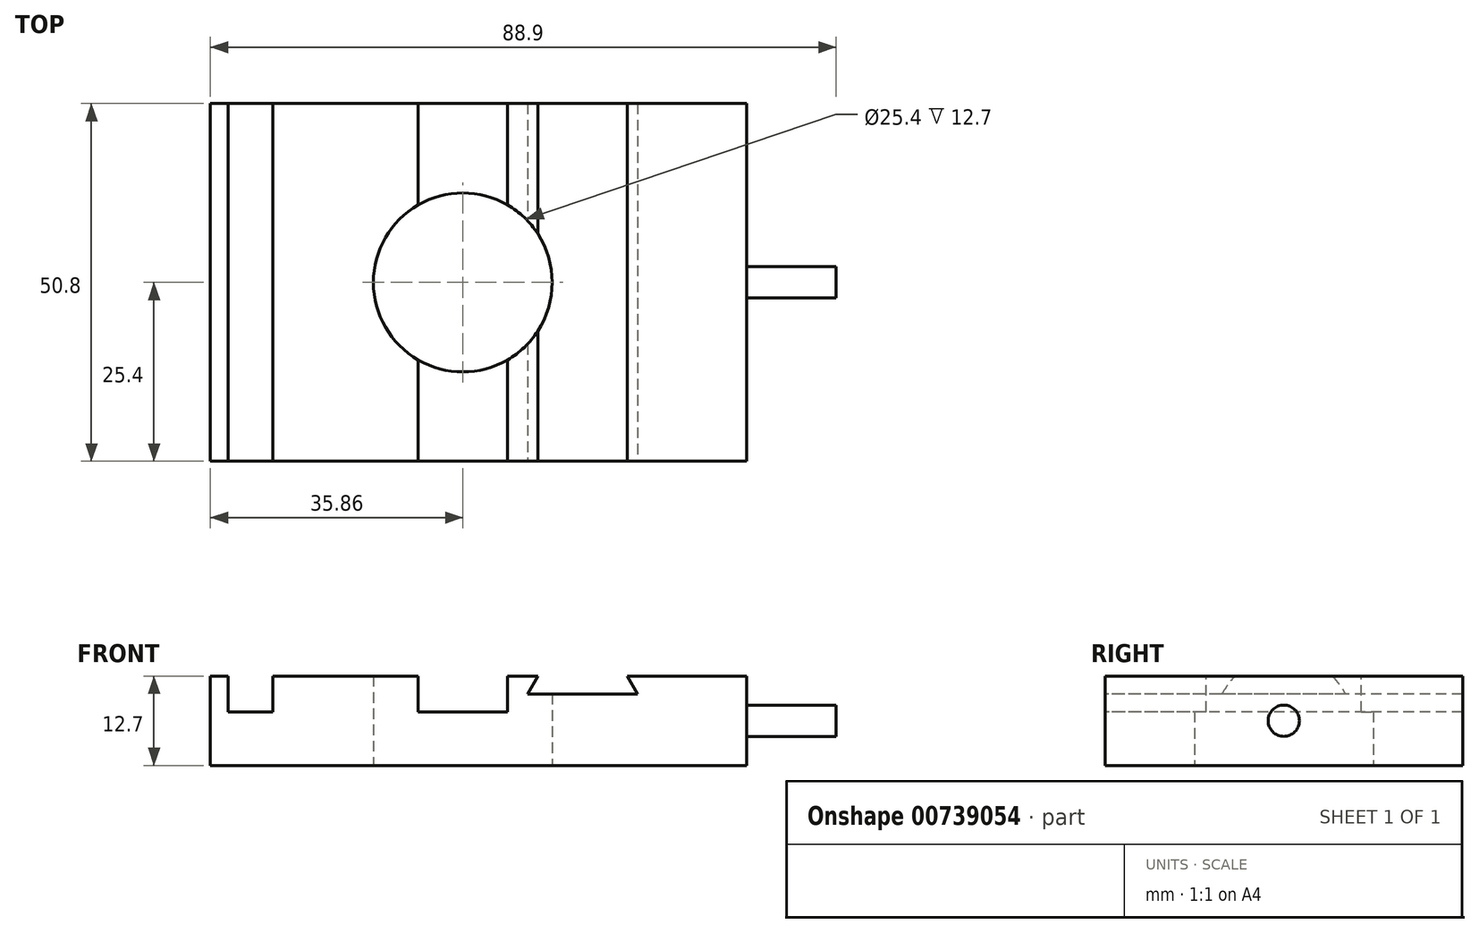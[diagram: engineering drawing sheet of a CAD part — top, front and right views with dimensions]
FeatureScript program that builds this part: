
annotation { "Feature Type Name" : "Feature", "Feature Type Description" : "" }
export const myFeature = defineFeature(function(context is Context, id is Id, definition is map)
    precondition{}
    {
        {
            var Q0;
            Q0=qCreatedBy(makeId("Top.planeOp"),FACE);
            var sketch = newSketch(context, id + "F0", { "sketchPlane" : qUnion([Q0])});
            skLineSegment(sketch, "E0.bottom", {"start": v(40.34, 25.4) * mm, "end": v(-35.86, 25.4) * mm});
            skLineSegment(sketch, "E0.top", {"start": v(40.34, -25.4) * mm, "end": v(-35.86, -25.4) * mm});
            skLineSegment(sketch, "E0.left", {"start": v(40.34, 25.4) * mm, "end": v(40.34, -25.4) * mm});
            skLineSegment(sketch, "E0.right", {"start": v(-35.86, 25.4) * mm, "end": v(-35.86, -25.4) * mm});
            skCircle(sketch, "E1", {"center": v(0, 0) * mm, "radius": 12.7 * mm});
            skSolve(sketch);
        }
        {
            var Q0;
            Q0=makeQuery(id+"F0.imprint","IMPRINT",FACE,{"disambiguationData":[TD([[makeQuery(id+"F0.imprint","IMPRINT",EDGE,{"derivedFrom":sQuery(id+"F0.wireOp",EDGE,"E0.bottom")}),1.0]])]});
            extrude(context, id + "F1", {"entities" : qUnion([Q0]), "depth" : 12.7 * mm, "offsetDistance" : 25 * mm});
        }
        {
            var Q0;
            Q0=makeQuery(id+"F1.opExtrude","CAP_FACE",FACE,{"disambiguationData":[OSD([sQuery(id+"F0.wireOp",EDGE,"E0.bottom"),sQuery(id+"F0.wireOp",EDGE,"E0.top"),sQuery(id+"F0.wireOp",EDGE,"E0.left"),sQuery(id+"F0.wireOp",EDGE,"E0.right"),sQuery(id+"F0.wireOp",EDGE,"E1")])],"isStart":false});
            var sketch = newSketch(context, id + "F2", { "sketchPlane" : qUnion([Q0])});
            skLineSegment(sketch, "E2.bottom", {"start": v(-33.32, 25.4) * mm, "end": v(-26.97, 25.4) * mm});
            skLineSegment(sketch, "E2.top", {"start": v(-33.32, -25.4) * mm, "end": v(-26.97, -25.4) * mm});
            skLineSegment(sketch, "E2.left", {"start": v(-33.32, 25.4) * mm, "end": v(-33.32, -25.4) * mm});
            skLineSegment(sketch, "E2.right", {"start": v(-26.97, 25.4) * mm, "end": v(-26.97, -25.4) * mm});
            skLineSegment(sketch, "E3", {"start": v(-6.35, 25.4) * mm, "end": v(-6.35, -25.4) * mm});
            skLineSegment(sketch, "E4", {"start": v(-6.35, -25.4) * mm, "end": v(6.35, -25.4) * mm});
            skLineSegment(sketch, "E5", {"start": v(6.35, -25.4) * mm, "end": v(6.35, 25.4) * mm});
            skPoint(sketch, "E6", {"position": v(0, 0) * mm});
            skLineSegment(sketch, "E7", {"start": v(6.35, 25.4) * mm, "end": v(-6.35, 25.4) * mm, "construction": true});
            skLineSegment(sketch, "E8", {"start": v(6.35, 25.4) * mm, "end": v(-6.35, 25.4) * mm});
            skLineSegment(sketch, "E9", {"start": v(0, 25.4) * mm, "end": v(0, -25.4) * mm, "construction": true});
            skSolve(sketch);
        }
        {
            var Q0;
            Q0=makeQuery(id+"F2.imprint","IMPRINT",FACE,{"disambiguationData":[TD([[makeQuery(id+"F2.imprint","IMPRINT",EDGE,{"derivedFrom":sQuery(id+"F2.wireOp",EDGE,"E2.bottom")}),1.0]])]});
            var Q1;
            {var subQ0=sQuery(id+"F2.wireOp",EDGE,"E4");Q1=makeQuery(id+"F2.imprint","IMPRINT",FACE,{"disambiguationData":[TD([[makeQuery(id+"F2.imprint","IMPRINT",EDGE,{"derivedFrom":subQ0}),-1.0]])]});}
            var Q2;
            {var subQ0=sQuery(id+"F2.wireOp",EDGE,"E8");Q2=makeQuery(id+"F2.imprint","IMPRINT",FACE,{"disambiguationData":[TD([[makeQuery(id+"F2.imprint","IMPRINT",EDGE,{"derivedFrom":subQ0}),1.0]])]});}
            extrude(context, id + "F3", {"entities" : qUnion([Q0, Q1, Q2]), "operationType" : NewBodyOperationType.REMOVE, "oppositeDirection" : true, "depth" : 5.08 * mm, "offsetDistance" : 25.4 * mm});
        }
        {
            var Q0;
            Q0=makeQuery(id+"F1.opExtrude","SWEPT_FACE",FACE,{"disambiguationData":[OSD([sQuery(id+"F0.wireOp",EDGE,"E0.top")])]});
            var sketch = newSketch(context, id + "F4", { "sketchPlane" : qUnion([Q0])});
            skLineSegment(sketch, "E10", {"start": v(10.64, 12.7) * mm, "end": v(9.18, 10.16) * mm});
            skLineSegment(sketch, "E11", {"start": v(9.18, 10.16) * mm, "end": v(24.81, 10.16) * mm});
            skLineSegment(sketch, "E12", {"start": v(24.81, 10.16) * mm, "end": v(23.34, 12.7) * mm});
            skLineSegment(sketch, "E13", {"start": v(23.34, 12.7) * mm, "end": v(10.64, 12.7) * mm});
            skLineSegment(sketch, "E14", {"start": v(17, 10.16) * mm, "end": v(17, 12.7) * mm, "construction": true});
            skSolve(sketch);
        }
        {
            var Q0;
            Q0=makeQuery(id+"F4.imprint","IMPRINT",FACE,{"disambiguationData":[TD([[makeQuery(id+"F4.imprint","IMPRINT",EDGE,{"derivedFrom":sQuery(id+"F4.wireOp",EDGE,"E10")}),1.0]])]});
            extrude(context, id + "F5", {"entities" : qUnion([Q0]), "operationType" : NewBodyOperationType.REMOVE, "endBound" : BoundingType.THROUGH_ALL, "oppositeDirection" : true, "depth" : 25.4 * mm, "offsetDistance" : 25.4 * mm});
        }
        {
            var Q0;
            Q0=makeQuery(id+"F1.opExtrude","SWEPT_FACE",FACE,{"disambiguationData":[OSD([sQuery(id+"F0.wireOp",EDGE,"E0.left")])]});
            var sketch = newSketch(context, id + "F6", { "sketchPlane" : qUnion([Q0])});
            skCircle(sketch, "E15", {"center": v(0, 6.35) * mm, "radius": 2.22 * mm});
            skPoint(sketch, "E15.centerSnap0", {"position": v(-25.4, 6.35) * mm});
            skSolve(sketch);
        }
        {
            var Q0;
            Q0=makeQuery(id+"F6.imprint","IMPRINT",FACE,{"disambiguationData":[TD([[makeQuery(id+"F6.imprint","IMPRINT",EDGE,{"derivedFrom":sQuery(id+"F6.wireOp",EDGE,"E15")}),1.0]])]});
            extrude(context, id + "F7", {"entities" : qUnion([Q0]), "operationType" : NewBodyOperationType.ADD, "depth" : 12.7 * mm, "offsetDistance" : 25.4 * mm});
        }
    });
